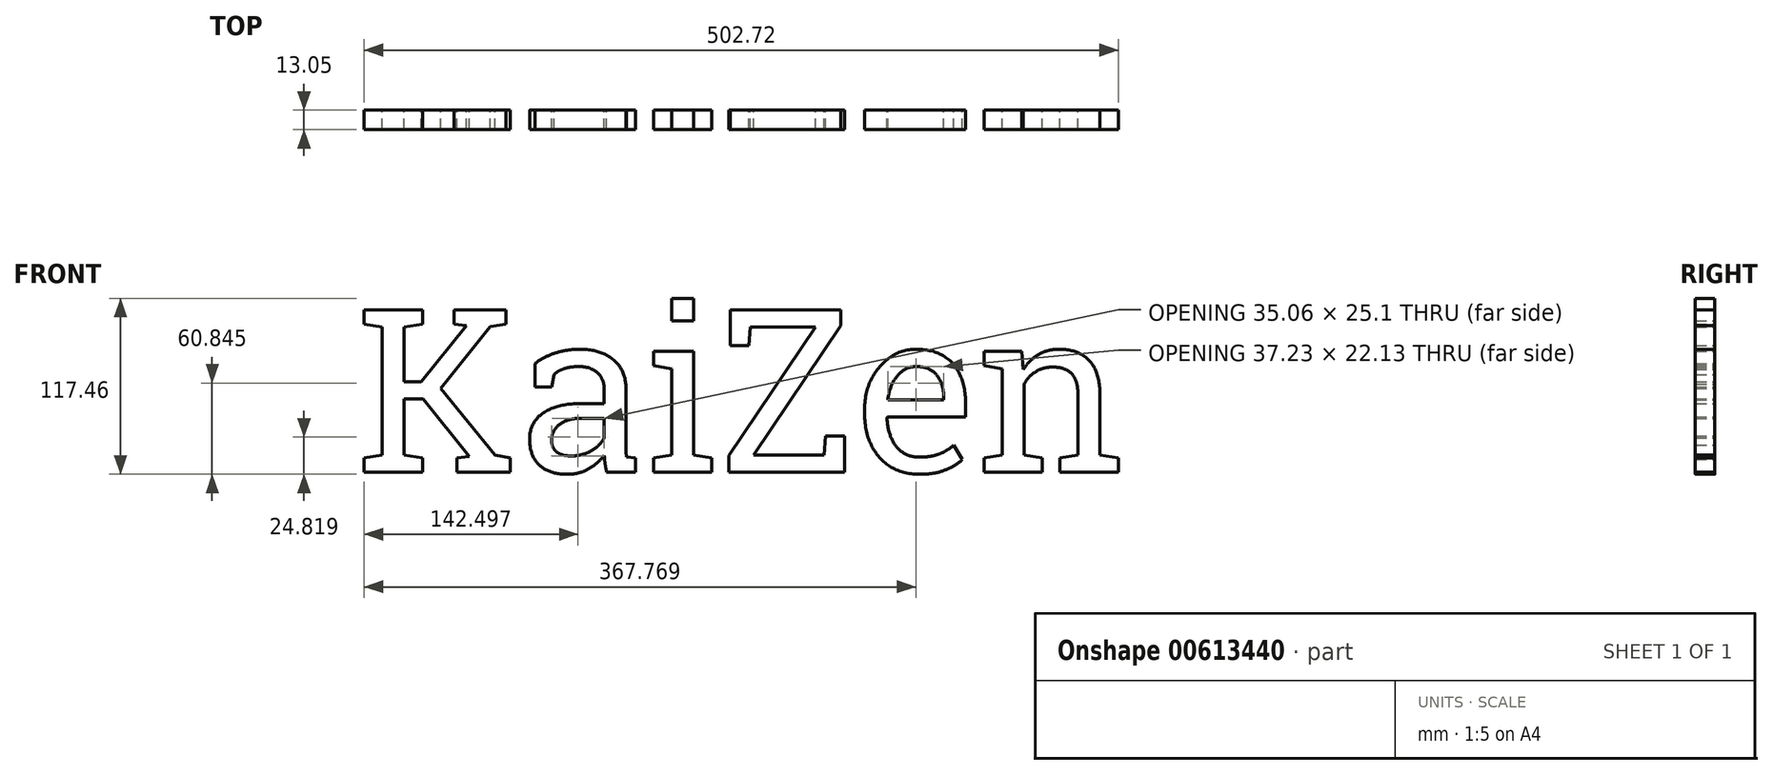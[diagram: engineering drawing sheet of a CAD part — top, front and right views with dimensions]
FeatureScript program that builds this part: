
annotation { "Feature Type Name" : "Feature", "Feature Type Description" : "" }
export const myFeature = defineFeature(function(context is Context, id is Id, definition is map)
    precondition{}
    {
        {
            var Q0;
            Q0=qCreatedBy(makeId("Front.planeOp"),FACE);
            var sketch = newSketch(context, id + "F0", { "sketchPlane" : qUnion([Q0])});
            skText(sketch, "E0", { "text": "KaiZen", "fontName": "RobotoSlab-Regular.ttf"});
            const initialGuessF0  = {"E0": [-0.05062, -0.04543, 1, 0, 0.10954]};
            skSetInitialGuess(sketch, initialGuessF0);
            skSolve(sketch);
        }
        {
            var Q0;
            Q0 = qSketchRegion(id + "F0", true);
            extrude(context, id + "F1", {"entities" : qUnion([Q0]), "depth" : 13.05 * mm, "offsetDistance" : 25.4 * mm});
        }
    });
